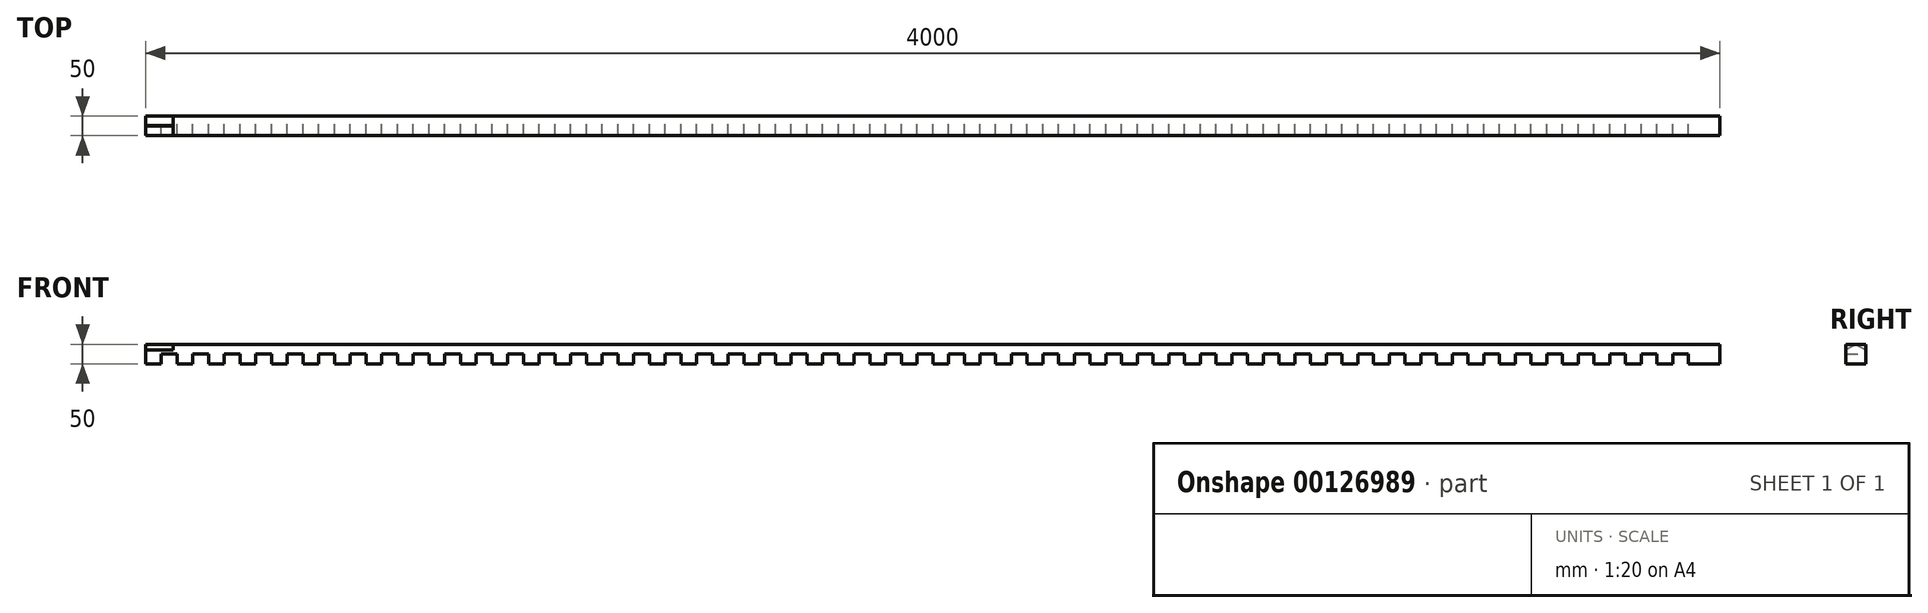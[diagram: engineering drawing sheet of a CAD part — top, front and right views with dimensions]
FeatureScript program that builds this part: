
annotation { "Feature Type Name" : "Feature", "Feature Type Description" : "" }
export const myFeature = defineFeature(function(context is Context, id is Id, definition is map)
    precondition{}
    {
        {
            var Q0;
            Q0=qCreatedBy(makeId("Front.planeOp"),FACE);
            var sketch = newSketch(context, id + "F0", { "sketchPlane" : qUnion([Q0])});
            skLineSegment(sketch, "E0.bottom", {"start": v(0, 0) * mm, "end": v(4000, 0) * mm});
            skLineSegment(sketch, "E0.top", {"start": v(0, 50) * mm, "end": v(4000, 50) * mm});
            skLineSegment(sketch, "E0.left", {"start": v(0, 0) * mm, "end": v(0, 50) * mm});
            skLineSegment(sketch, "E0.right", {"start": v(4000, 0) * mm, "end": v(4000, 50) * mm});
            skPoint(sketch, "E1.start.orphan", {"position": v(0, 25) * mm});
            skLineSegment(sketch, "E2.right", {"start": v(40, 0) * mm, "end": v(40, 25) * mm});
            skLineSegment(sketch, "E3.bottom", {"start": v(40, 25) * mm, "end": v(80, 25) * mm});
            skLineSegment(sketch, "E3.top", {"start": v(40, 0) * mm, "end": v(80, 0) * mm});
            skLineSegment(sketch, "E3.left", {"start": v(40, 25) * mm, "end": v(40, 0) * mm});
            skLineSegment(sketch, "E3.right", {"start": v(80, 25) * mm, "end": v(80, 0) * mm});
            skLineSegment(sketch, "E4.1.0.0", {"start": v(160, 25) * mm, "end": v(160, 0) * mm});
            skLineSegment(sketch, "E4.1.0.1", {"start": v(120, 0) * mm, "end": v(160, 0) * mm});
            skLineSegment(sketch, "E4.1.0.2", {"start": v(120, 25) * mm, "end": v(120, 0) * mm});
            skLineSegment(sketch, "E4.1.0.3", {"start": v(120, 25) * mm, "end": v(160, 25) * mm});
            skLineSegment(sketch, "E4.2.0.0", {"start": v(240, 25) * mm, "end": v(240, 0) * mm});
            skLineSegment(sketch, "E4.2.0.1", {"start": v(200, 0) * mm, "end": v(240, 0) * mm});
            skLineSegment(sketch, "E4.2.0.2", {"start": v(200, 25) * mm, "end": v(200, 0) * mm});
            skLineSegment(sketch, "E4.2.0.3", {"start": v(200, 25) * mm, "end": v(240, 25) * mm});
            skLineSegment(sketch, "E4.3.0.0", {"start": v(320, 25) * mm, "end": v(320, 0) * mm});
            skLineSegment(sketch, "E4.3.0.1", {"start": v(280, 0) * mm, "end": v(320, 0) * mm});
            skLineSegment(sketch, "E4.3.0.2", {"start": v(280, 25) * mm, "end": v(280, 0) * mm});
            skLineSegment(sketch, "E4.3.0.3", {"start": v(280, 25) * mm, "end": v(320, 25) * mm});
            skLineSegment(sketch, "E4.4.0.0", {"start": v(400, 25) * mm, "end": v(400, 0) * mm});
            skLineSegment(sketch, "E4.4.0.1", {"start": v(360, 0) * mm, "end": v(400, 0) * mm});
            skLineSegment(sketch, "E4.4.0.2", {"start": v(360, 25) * mm, "end": v(360, 0) * mm});
            skLineSegment(sketch, "E4.4.0.3", {"start": v(360, 25) * mm, "end": v(400, 25) * mm});
            skLineSegment(sketch, "E4.5.0.0", {"start": v(480, 25) * mm, "end": v(480, 0) * mm});
            skLineSegment(sketch, "E4.5.0.1", {"start": v(440, 0) * mm, "end": v(480, 0) * mm});
            skLineSegment(sketch, "E4.5.0.2", {"start": v(440, 25) * mm, "end": v(440, 0) * mm});
            skLineSegment(sketch, "E4.5.0.3", {"start": v(440, 25) * mm, "end": v(480, 25) * mm});
            skLineSegment(sketch, "E4.6.0.0", {"start": v(560, 25) * mm, "end": v(560, 0) * mm});
            skLineSegment(sketch, "E4.6.0.1", {"start": v(520, 0) * mm, "end": v(560, 0) * mm});
            skLineSegment(sketch, "E4.6.0.2", {"start": v(520, 25) * mm, "end": v(520, 0) * mm});
            skLineSegment(sketch, "E4.6.0.3", {"start": v(520, 25) * mm, "end": v(560, 25) * mm});
            skLineSegment(sketch, "E4.7.0.0", {"start": v(640, 25) * mm, "end": v(640, 0) * mm});
            skLineSegment(sketch, "E4.7.0.1", {"start": v(600, 0) * mm, "end": v(640, 0) * mm});
            skLineSegment(sketch, "E4.7.0.2", {"start": v(600, 25) * mm, "end": v(600, 0) * mm});
            skLineSegment(sketch, "E4.7.0.3", {"start": v(600, 25) * mm, "end": v(640, 25) * mm});
            skLineSegment(sketch, "E4.8.0.0", {"start": v(720, 25) * mm, "end": v(720, 0) * mm});
            skLineSegment(sketch, "E4.8.0.1", {"start": v(680, 0) * mm, "end": v(720, 0) * mm});
            skLineSegment(sketch, "E4.8.0.2", {"start": v(680, 25) * mm, "end": v(680, 0) * mm});
            skLineSegment(sketch, "E4.8.0.3", {"start": v(680, 25) * mm, "end": v(720, 25) * mm});
            skLineSegment(sketch, "E4.9.0.0", {"start": v(800, 25) * mm, "end": v(800, 0) * mm});
            skLineSegment(sketch, "E4.9.0.1", {"start": v(760, 0) * mm, "end": v(800, 0) * mm});
            skLineSegment(sketch, "E4.9.0.2", {"start": v(760, 25) * mm, "end": v(760, 0) * mm});
            skLineSegment(sketch, "E4.9.0.3", {"start": v(760, 25) * mm, "end": v(800, 25) * mm});
            skLineSegment(sketch, "E4.10.0.0", {"start": v(880, 25) * mm, "end": v(880, 0) * mm});
            skLineSegment(sketch, "E4.10.0.1", {"start": v(840, 0) * mm, "end": v(880, 0) * mm});
            skLineSegment(sketch, "E4.10.0.2", {"start": v(840, 25) * mm, "end": v(840, 0) * mm});
            skLineSegment(sketch, "E4.10.0.3", {"start": v(840, 25) * mm, "end": v(880, 25) * mm});
            skLineSegment(sketch, "E4.11.0.0", {"start": v(960, 25) * mm, "end": v(960, 0) * mm});
            skLineSegment(sketch, "E4.11.0.1", {"start": v(920, 0) * mm, "end": v(960, 0) * mm});
            skLineSegment(sketch, "E4.11.0.2", {"start": v(920, 25) * mm, "end": v(920, 0) * mm});
            skLineSegment(sketch, "E4.11.0.3", {"start": v(920, 25) * mm, "end": v(960, 25) * mm});
            skLineSegment(sketch, "E4.12.0.0", {"start": v(1040, 25) * mm, "end": v(1040, 0) * mm});
            skLineSegment(sketch, "E4.12.0.1", {"start": v(1000, 0) * mm, "end": v(1040, 0) * mm});
            skLineSegment(sketch, "E4.12.0.2", {"start": v(1000, 25) * mm, "end": v(1000, 0) * mm});
            skLineSegment(sketch, "E4.12.0.3", {"start": v(1000, 25) * mm, "end": v(1040, 25) * mm});
            skLineSegment(sketch, "E4.13.0.0", {"start": v(1120, 25) * mm, "end": v(1120, 0) * mm});
            skLineSegment(sketch, "E4.13.0.1", {"start": v(1080, 0) * mm, "end": v(1120, 0) * mm});
            skLineSegment(sketch, "E4.13.0.2", {"start": v(1080, 25) * mm, "end": v(1080, 0) * mm});
            skLineSegment(sketch, "E4.13.0.3", {"start": v(1080, 25) * mm, "end": v(1120, 25) * mm});
            skLineSegment(sketch, "E4.14.0.0", {"start": v(1200, 25) * mm, "end": v(1200, 0) * mm});
            skLineSegment(sketch, "E4.14.0.1", {"start": v(1160, 0) * mm, "end": v(1200, 0) * mm});
            skLineSegment(sketch, "E4.14.0.2", {"start": v(1160, 25) * mm, "end": v(1160, 0) * mm});
            skLineSegment(sketch, "E4.14.0.3", {"start": v(1160, 25) * mm, "end": v(1200, 25) * mm});
            skLineSegment(sketch, "E4.15.0.0", {"start": v(1280, 25) * mm, "end": v(1280, 0) * mm});
            skLineSegment(sketch, "E4.15.0.1", {"start": v(1240, 0) * mm, "end": v(1280, 0) * mm});
            skLineSegment(sketch, "E4.15.0.2", {"start": v(1240, 25) * mm, "end": v(1240, 0) * mm});
            skLineSegment(sketch, "E4.15.0.3", {"start": v(1240, 25) * mm, "end": v(1280, 25) * mm});
            skLineSegment(sketch, "E4.16.0.0", {"start": v(1360, 25) * mm, "end": v(1360, 0) * mm});
            skLineSegment(sketch, "E4.16.0.1", {"start": v(1320, 0) * mm, "end": v(1360, 0) * mm});
            skLineSegment(sketch, "E4.16.0.2", {"start": v(1320, 25) * mm, "end": v(1320, 0) * mm});
            skLineSegment(sketch, "E4.16.0.3", {"start": v(1320, 25) * mm, "end": v(1360, 25) * mm});
            skLineSegment(sketch, "E4.17.0.0", {"start": v(1440, 25) * mm, "end": v(1440, 0) * mm});
            skLineSegment(sketch, "E4.17.0.1", {"start": v(1400, 0) * mm, "end": v(1440, 0) * mm});
            skLineSegment(sketch, "E4.17.0.2", {"start": v(1400, 25) * mm, "end": v(1400, 0) * mm});
            skLineSegment(sketch, "E4.17.0.3", {"start": v(1400, 25) * mm, "end": v(1440, 25) * mm});
            skLineSegment(sketch, "E4.18.0.0", {"start": v(1520, 25) * mm, "end": v(1520, 0) * mm});
            skLineSegment(sketch, "E4.18.0.1", {"start": v(1480, 0) * mm, "end": v(1520, 0) * mm});
            skLineSegment(sketch, "E4.18.0.2", {"start": v(1480, 25) * mm, "end": v(1480, 0) * mm});
            skLineSegment(sketch, "E4.18.0.3", {"start": v(1480, 25) * mm, "end": v(1520, 25) * mm});
            skLineSegment(sketch, "E4.19.0.0", {"start": v(1600, 25) * mm, "end": v(1600, 0) * mm});
            skLineSegment(sketch, "E4.19.0.1", {"start": v(1560, 0) * mm, "end": v(1600, 0) * mm});
            skLineSegment(sketch, "E4.19.0.2", {"start": v(1560, 25) * mm, "end": v(1560, 0) * mm});
            skLineSegment(sketch, "E4.19.0.3", {"start": v(1560, 25) * mm, "end": v(1600, 25) * mm});
            skLineSegment(sketch, "E4.20.0.0", {"start": v(1680, 25) * mm, "end": v(1680, 0) * mm});
            skLineSegment(sketch, "E4.20.0.1", {"start": v(1640, 0) * mm, "end": v(1680, 0) * mm});
            skLineSegment(sketch, "E4.20.0.2", {"start": v(1640, 25) * mm, "end": v(1640, 0) * mm});
            skLineSegment(sketch, "E4.20.0.3", {"start": v(1640, 25) * mm, "end": v(1680, 25) * mm});
            skLineSegment(sketch, "E4.21.0.0", {"start": v(1760, 25) * mm, "end": v(1760, 0) * mm});
            skLineSegment(sketch, "E4.21.0.1", {"start": v(1720, 0) * mm, "end": v(1760, 0) * mm});
            skLineSegment(sketch, "E4.21.0.2", {"start": v(1720, 25) * mm, "end": v(1720, 0) * mm});
            skLineSegment(sketch, "E4.21.0.3", {"start": v(1720, 25) * mm, "end": v(1760, 25) * mm});
            skLineSegment(sketch, "E4.22.0.0", {"start": v(1840, 25) * mm, "end": v(1840, 0) * mm});
            skLineSegment(sketch, "E4.22.0.1", {"start": v(1800, 0) * mm, "end": v(1840, 0) * mm});
            skLineSegment(sketch, "E4.22.0.2", {"start": v(1800, 25) * mm, "end": v(1800, 0) * mm});
            skLineSegment(sketch, "E4.22.0.3", {"start": v(1800, 25) * mm, "end": v(1840, 25) * mm});
            skLineSegment(sketch, "E4.23.0.0", {"start": v(1920, 25) * mm, "end": v(1920, 0) * mm});
            skLineSegment(sketch, "E4.23.0.1", {"start": v(1880, 0) * mm, "end": v(1920, 0) * mm});
            skLineSegment(sketch, "E4.23.0.2", {"start": v(1880, 25) * mm, "end": v(1880, 0) * mm});
            skLineSegment(sketch, "E4.23.0.3", {"start": v(1880, 25) * mm, "end": v(1920, 25) * mm});
            skLineSegment(sketch, "E4.24.0.0", {"start": v(2000, 25) * mm, "end": v(2000, 0) * mm});
            skLineSegment(sketch, "E4.24.0.1", {"start": v(1960, 0) * mm, "end": v(2000, 0) * mm});
            skLineSegment(sketch, "E4.24.0.2", {"start": v(1960, 25) * mm, "end": v(1960, 0) * mm});
            skLineSegment(sketch, "E4.24.0.3", {"start": v(1960, 25) * mm, "end": v(2000, 25) * mm});
            skLineSegment(sketch, "E4.25.0.0", {"start": v(2080, 25) * mm, "end": v(2080, 0) * mm});
            skLineSegment(sketch, "E4.25.0.1", {"start": v(2040, 0) * mm, "end": v(2080, 0) * mm});
            skLineSegment(sketch, "E4.25.0.2", {"start": v(2040, 25) * mm, "end": v(2040, 0) * mm});
            skLineSegment(sketch, "E4.25.0.3", {"start": v(2040, 25) * mm, "end": v(2080, 25) * mm});
            skLineSegment(sketch, "E4.26.0.0", {"start": v(2160, 25) * mm, "end": v(2160, 0) * mm});
            skLineSegment(sketch, "E4.26.0.1", {"start": v(2120, 0) * mm, "end": v(2160, 0) * mm});
            skLineSegment(sketch, "E4.26.0.2", {"start": v(2120, 25) * mm, "end": v(2120, 0) * mm});
            skLineSegment(sketch, "E4.26.0.3", {"start": v(2120, 25) * mm, "end": v(2160, 25) * mm});
            skLineSegment(sketch, "E4.27.0.0", {"start": v(2240, 25) * mm, "end": v(2240, 0) * mm});
            skLineSegment(sketch, "E4.27.0.1", {"start": v(2200, 0) * mm, "end": v(2240, 0) * mm});
            skLineSegment(sketch, "E4.27.0.2", {"start": v(2200, 25) * mm, "end": v(2200, 0) * mm});
            skLineSegment(sketch, "E4.27.0.3", {"start": v(2200, 25) * mm, "end": v(2240, 25) * mm});
            skLineSegment(sketch, "E4.28.0.0", {"start": v(2320, 25) * mm, "end": v(2320, 0) * mm});
            skLineSegment(sketch, "E4.28.0.1", {"start": v(2280, 0) * mm, "end": v(2320, 0) * mm});
            skLineSegment(sketch, "E4.28.0.2", {"start": v(2280, 25) * mm, "end": v(2280, 0) * mm});
            skLineSegment(sketch, "E4.28.0.3", {"start": v(2280, 25) * mm, "end": v(2320, 25) * mm});
            skLineSegment(sketch, "E4.29.0.0", {"start": v(2400, 25) * mm, "end": v(2400, 0) * mm});
            skLineSegment(sketch, "E4.29.0.1", {"start": v(2360, 0) * mm, "end": v(2400, 0) * mm});
            skLineSegment(sketch, "E4.29.0.2", {"start": v(2360, 25) * mm, "end": v(2360, 0) * mm});
            skLineSegment(sketch, "E4.29.0.3", {"start": v(2360, 25) * mm, "end": v(2400, 25) * mm});
            skLineSegment(sketch, "E4.30.0.0", {"start": v(2480, 25) * mm, "end": v(2480, 0) * mm});
            skLineSegment(sketch, "E4.30.0.1", {"start": v(2440, 0) * mm, "end": v(2480, 0) * mm});
            skLineSegment(sketch, "E4.30.0.2", {"start": v(2440, 25) * mm, "end": v(2440, 0) * mm});
            skLineSegment(sketch, "E4.30.0.3", {"start": v(2440, 25) * mm, "end": v(2480, 25) * mm});
            skLineSegment(sketch, "E4.31.0.0", {"start": v(2560, 25) * mm, "end": v(2560, 0) * mm});
            skLineSegment(sketch, "E4.31.0.1", {"start": v(2520, 0) * mm, "end": v(2560, 0) * mm});
            skLineSegment(sketch, "E4.31.0.2", {"start": v(2520, 25) * mm, "end": v(2520, 0) * mm});
            skLineSegment(sketch, "E4.31.0.3", {"start": v(2520, 25) * mm, "end": v(2560, 25) * mm});
            skLineSegment(sketch, "E4.32.0.0", {"start": v(2640, 25) * mm, "end": v(2640, 0) * mm});
            skLineSegment(sketch, "E4.32.0.1", {"start": v(2600, 0) * mm, "end": v(2640, 0) * mm});
            skLineSegment(sketch, "E4.32.0.2", {"start": v(2600, 25) * mm, "end": v(2600, 0) * mm});
            skLineSegment(sketch, "E4.32.0.3", {"start": v(2600, 25) * mm, "end": v(2640, 25) * mm});
            skLineSegment(sketch, "E4.33.0.0", {"start": v(2720, 25) * mm, "end": v(2720, 0) * mm});
            skLineSegment(sketch, "E4.33.0.1", {"start": v(2680, 0) * mm, "end": v(2720, 0) * mm});
            skLineSegment(sketch, "E4.33.0.2", {"start": v(2680, 25) * mm, "end": v(2680, 0) * mm});
            skLineSegment(sketch, "E4.33.0.3", {"start": v(2680, 25) * mm, "end": v(2720, 25) * mm});
            skLineSegment(sketch, "E4.34.0.0", {"start": v(2800, 25) * mm, "end": v(2800, 0) * mm});
            skLineSegment(sketch, "E4.34.0.1", {"start": v(2760, 0) * mm, "end": v(2800, 0) * mm});
            skLineSegment(sketch, "E4.34.0.2", {"start": v(2760, 25) * mm, "end": v(2760, 0) * mm});
            skLineSegment(sketch, "E4.34.0.3", {"start": v(2760, 25) * mm, "end": v(2800, 25) * mm});
            skLineSegment(sketch, "E4.35.0.0", {"start": v(2880, 25) * mm, "end": v(2880, 0) * mm});
            skLineSegment(sketch, "E4.35.0.1", {"start": v(2840, 0) * mm, "end": v(2880, 0) * mm});
            skLineSegment(sketch, "E4.35.0.2", {"start": v(2840, 25) * mm, "end": v(2840, 0) * mm});
            skLineSegment(sketch, "E4.35.0.3", {"start": v(2840, 25) * mm, "end": v(2880, 25) * mm});
            skLineSegment(sketch, "E4.36.0.0", {"start": v(2960, 25) * mm, "end": v(2960, 0) * mm});
            skLineSegment(sketch, "E4.36.0.1", {"start": v(2920, 0) * mm, "end": v(2960, 0) * mm});
            skLineSegment(sketch, "E4.36.0.2", {"start": v(2920, 25) * mm, "end": v(2920, 0) * mm});
            skLineSegment(sketch, "E4.36.0.3", {"start": v(2920, 25) * mm, "end": v(2960, 25) * mm});
            skLineSegment(sketch, "E4.37.0.0", {"start": v(3040, 25) * mm, "end": v(3040, 0) * mm});
            skLineSegment(sketch, "E4.37.0.1", {"start": v(3000, 0) * mm, "end": v(3040, 0) * mm});
            skLineSegment(sketch, "E4.37.0.2", {"start": v(3000, 25) * mm, "end": v(3000, 0) * mm});
            skLineSegment(sketch, "E4.37.0.3", {"start": v(3000, 25) * mm, "end": v(3040, 25) * mm});
            skLineSegment(sketch, "E4.38.0.0", {"start": v(3120, 25) * mm, "end": v(3120, 0) * mm});
            skLineSegment(sketch, "E4.38.0.1", {"start": v(3080, 0) * mm, "end": v(3120, 0) * mm});
            skLineSegment(sketch, "E4.38.0.2", {"start": v(3080, 25) * mm, "end": v(3080, 0) * mm});
            skLineSegment(sketch, "E4.38.0.3", {"start": v(3080, 25) * mm, "end": v(3120, 25) * mm});
            skLineSegment(sketch, "E4.39.0.0", {"start": v(3200, 25) * mm, "end": v(3200, 0) * mm});
            skLineSegment(sketch, "E4.39.0.1", {"start": v(3160, 0) * mm, "end": v(3200, 0) * mm});
            skLineSegment(sketch, "E4.39.0.2", {"start": v(3160, 25) * mm, "end": v(3160, 0) * mm});
            skLineSegment(sketch, "E4.39.0.3", {"start": v(3160, 25) * mm, "end": v(3200, 25) * mm});
            skLineSegment(sketch, "E4.40.0.0", {"start": v(3280, 25) * mm, "end": v(3280, 0) * mm});
            skLineSegment(sketch, "E4.40.0.1", {"start": v(3240, 0) * mm, "end": v(3280, 0) * mm});
            skLineSegment(sketch, "E4.40.0.2", {"start": v(3240, 25) * mm, "end": v(3240, 0) * mm});
            skLineSegment(sketch, "E4.40.0.3", {"start": v(3240, 25) * mm, "end": v(3280, 25) * mm});
            skLineSegment(sketch, "E4.41.0.0", {"start": v(3360, 25) * mm, "end": v(3360, 0) * mm});
            skLineSegment(sketch, "E4.41.0.1", {"start": v(3320, 0) * mm, "end": v(3360, 0) * mm});
            skLineSegment(sketch, "E4.41.0.2", {"start": v(3320, 25) * mm, "end": v(3320, 0) * mm});
            skLineSegment(sketch, "E4.41.0.3", {"start": v(3320, 25) * mm, "end": v(3360, 25) * mm});
            skLineSegment(sketch, "E4.42.0.0", {"start": v(3440, 25) * mm, "end": v(3440, 0) * mm});
            skLineSegment(sketch, "E4.42.0.1", {"start": v(3400, 0) * mm, "end": v(3440, 0) * mm});
            skLineSegment(sketch, "E4.42.0.2", {"start": v(3400, 25) * mm, "end": v(3400, 0) * mm});
            skLineSegment(sketch, "E4.42.0.3", {"start": v(3400, 25) * mm, "end": v(3440, 25) * mm});
            skLineSegment(sketch, "E4.43.0.0", {"start": v(3520, 25) * mm, "end": v(3520, 0) * mm});
            skLineSegment(sketch, "E4.43.0.1", {"start": v(3480, 0) * mm, "end": v(3520, 0) * mm});
            skLineSegment(sketch, "E4.43.0.2", {"start": v(3480, 25) * mm, "end": v(3480, 0) * mm});
            skLineSegment(sketch, "E4.43.0.3", {"start": v(3480, 25) * mm, "end": v(3520, 25) * mm});
            skLineSegment(sketch, "E4.44.0.0", {"start": v(3600, 25) * mm, "end": v(3600, 0) * mm});
            skLineSegment(sketch, "E4.44.0.1", {"start": v(3560, 0) * mm, "end": v(3600, 0) * mm});
            skLineSegment(sketch, "E4.44.0.2", {"start": v(3560, 25) * mm, "end": v(3560, 0) * mm});
            skLineSegment(sketch, "E4.44.0.3", {"start": v(3560, 25) * mm, "end": v(3600, 25) * mm});
            skLineSegment(sketch, "E4.45.0.0", {"start": v(3680, 25) * mm, "end": v(3680, 0) * mm});
            skLineSegment(sketch, "E4.45.0.1", {"start": v(3640, 0) * mm, "end": v(3680, 0) * mm});
            skLineSegment(sketch, "E4.45.0.2", {"start": v(3640, 25) * mm, "end": v(3640, 0) * mm});
            skLineSegment(sketch, "E4.45.0.3", {"start": v(3640, 25) * mm, "end": v(3680, 25) * mm});
            skLineSegment(sketch, "E4.46.0.0", {"start": v(3760, 25) * mm, "end": v(3760, 0) * mm});
            skLineSegment(sketch, "E4.46.0.1", {"start": v(3720, 0) * mm, "end": v(3760, 0) * mm});
            skLineSegment(sketch, "E4.46.0.2", {"start": v(3720, 25) * mm, "end": v(3720, 0) * mm});
            skLineSegment(sketch, "E4.46.0.3", {"start": v(3720, 25) * mm, "end": v(3760, 25) * mm});
            skLineSegment(sketch, "E4.47.0.0", {"start": v(3840, 25) * mm, "end": v(3840, 0) * mm});
            skLineSegment(sketch, "E4.47.0.1", {"start": v(3800, 0) * mm, "end": v(3840, 0) * mm});
            skLineSegment(sketch, "E4.47.0.2", {"start": v(3800, 25) * mm, "end": v(3800, 0) * mm});
            skLineSegment(sketch, "E4.47.0.3", {"start": v(3800, 25) * mm, "end": v(3840, 25) * mm});
            skLineSegment(sketch, "E4.48.0.0", {"start": v(3920, 25) * mm, "end": v(3920, 0) * mm});
            skLineSegment(sketch, "E4.48.0.1", {"start": v(3880, 0) * mm, "end": v(3920, 0) * mm});
            skLineSegment(sketch, "E4.48.0.2", {"start": v(3880, 25) * mm, "end": v(3880, 0) * mm});
            skLineSegment(sketch, "E4.48.0.3", {"start": v(3880, 25) * mm, "end": v(3920, 25) * mm});
            skLineSegment(sketch, "E4.direction1", {"start": v(80, 0) * mm, "end": v(160, 0) * mm, "construction": true});
            skSolve(sketch);
        }
        {
            var Q0;
            Q0=makeQuery(id+"F0.imprint","IMPRINT",FACE,{"disambiguationData":[TD([[makeQuery(id+"F0.imprint","IMPRINT",EDGE,{"derivedFrom":sQuery(id+"F0.wireOp",EDGE,"E0.top")}),-1.0]])]});
            extrude(context, id + "F1", {"entities" : qUnion([Q0]), "endBound" : BoundingType.SYMMETRIC, "depth" : 50 * mm});
        }
        {
            var Q0;
            Q0=qCreatedBy(makeId("Right.planeOp"),FACE);
            var sketch = newSketch(context, id + "F2", { "sketchPlane" : qUnion([Q0])});
            skLineSegment(sketch, "E5", {"start": v(-25.12, 35.59) * mm, "end": v(-25.12, 50.16) * mm});
            skLineSegment(sketch, "E6", {"start": v(-25.12, 50.16) * mm, "end": v(25.36, 50.16) * mm});
            skLineSegment(sketch, "E7", {"start": v(25.36, 50.16) * mm, "end": v(25.36, 35.59) * mm});
            skLineSegment(sketch, "E8", {"start": v(0, 50.16) * mm, "end": v(0, 50.1) * mm});
            skPoint(sketch, "E8.startSnap0", {"position": v(0.12, 50.16) * mm});
            skLineSegment(sketch, "E9", {"start": v(0.12, 50.16) * mm, "end": v(25.36, 35.59) * mm});
            skLineSegment(sketch, "E10", {"start": v(0.12, 50.16) * mm, "end": v(-25.12, 35.59) * mm});
            skPoint(sketch, "E11.orphan", {"position": v(25.36, 0) * mm});
            skSolve(sketch);
        }
        {
            var Q0;
            {var subQ0=sQuery(id+"F2.wireOp",EDGE,"E5");Q0=makeQuery(id+"F2.imprint","IMPRINT",FACE,{"disambiguationData":[TD([[makeQuery(id+"F2.imprint","IMPRINT",EDGE,{"derivedFrom":subQ0}),-1.0]])]});}
            var Q1;
            {var subQ0=sQuery(id+"F2.wireOp",EDGE,"E7");Q1=makeQuery(id+"F2.imprint","IMPRINT",FACE,{"disambiguationData":[TD([[makeQuery(id+"F2.imprint","IMPRINT",EDGE,{"derivedFrom":subQ0}),-1.0]])]});}
            extrude(context, id + "F3", {"entities" : qUnion([Q0, Q1]), "operationType" : NewBodyOperationType.REMOVE, "depth" : 70 * mm});
        }
    });
